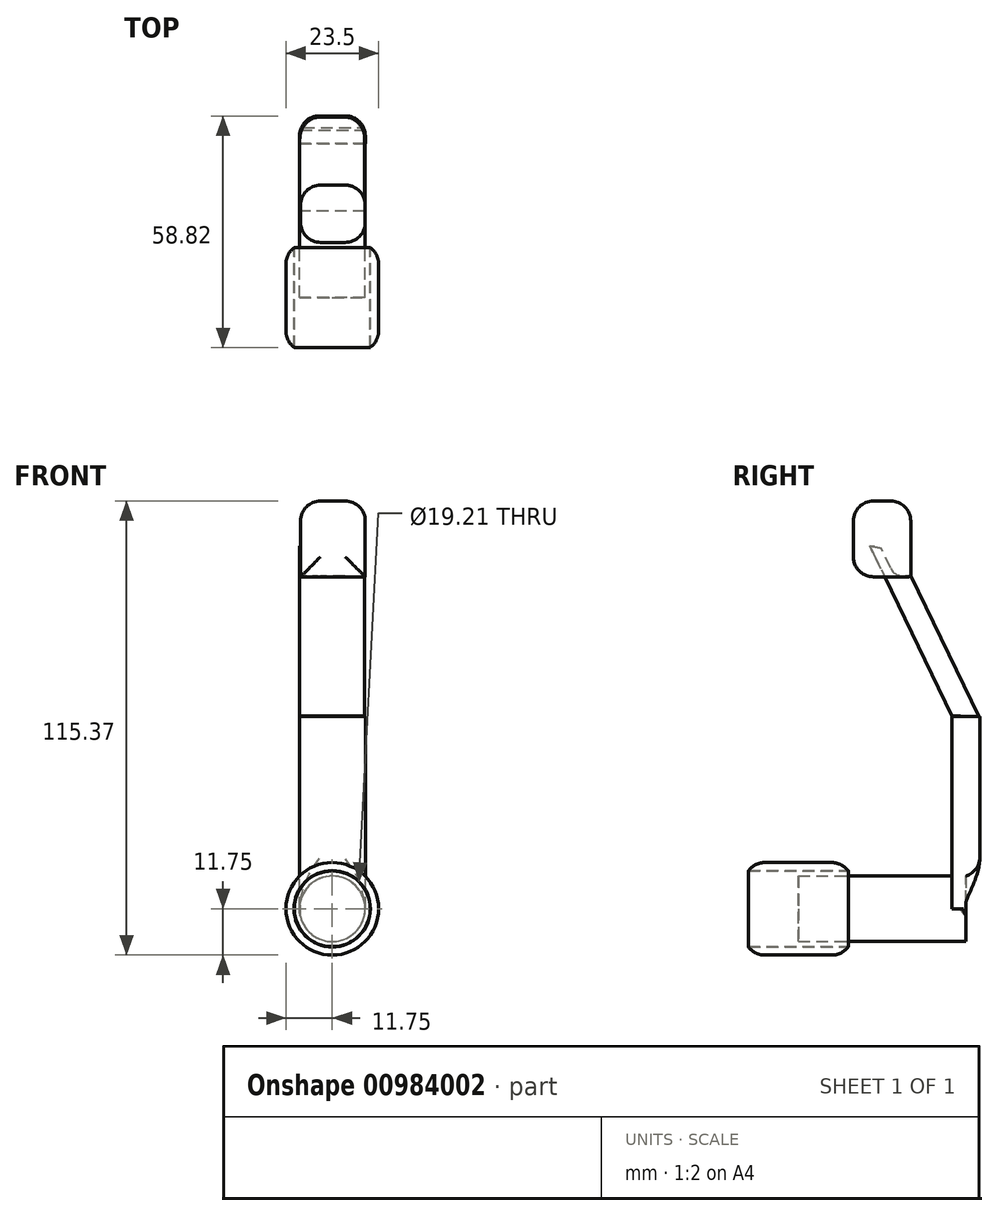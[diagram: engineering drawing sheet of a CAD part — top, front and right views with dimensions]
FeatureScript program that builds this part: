
annotation { "Feature Type Name" : "Feature", "Feature Type Description" : "" }
export const myFeature = defineFeature(function(context is Context, id is Id, definition is map)
    precondition{}
    {
        {
            var Q0;
            Q0=qCreatedBy(makeId("Front.planeOp"),FACE);
            var sketch = newSketch(context, id + "F0", { "sketchPlane" : qUnion([Q0])});
            skCircle(sketch, "E0", {"center": v(0, 0) * mm, "radius": 8.33 * mm});
            skSolve(sketch);
        }
        {
            var Q0;
            Q0 = qSketchRegion(id + "F0", true);
            extrude(context, id + "F1", {"entities" : qUnion([Q0]), "endBound" : BoundingType.SYMMETRIC, "depth" : 42.58 * mm, "offsetDistance" : 25.4 * mm});
        }
        {
            var Q0;
            Q0=makeQuery(id+"F1.opExtrude","CAP_FACE",FACE,{"disambiguationData":[OSD([sQuery(id+"F0.wireOp",EDGE,"E0")])],"isStart":false});
            var sketch = newSketch(context, id + "F2", { "sketchPlane" : qUnion([Q0])});
            skCircle(sketch, "E1", {"center": v(0, 0) * mm, "radius": 11.75 * mm});
            skCircle(sketch, "E2", {"center": v(0, 0) * mm, "radius": 9.6 * mm});
            skSolve(sketch);
        }
        {
            var Q0;
            Q0 = qSketchRegion(id + "F2", true);
            extrude(context, id + "F3", {"entities" : qUnion([Q0]), "endBound" : BoundingType.SYMMETRIC, "depth" : 25.4 * mm, "offsetDistance" : 25.4 * mm});
        }
        {
            var Q0;
            Q0=makeQuery(id+"F1.opExtrude","CAP_FACE",FACE,{"disambiguationData":[OSD([sQuery(id+"F0.wireOp",EDGE,"E0")])],"isStart":false});
            var sketch = newSketch(context, id + "F4", { "sketchPlane" : qUnion([Q0])});
            skCircle(sketch, "E3", {"center": v(0, 0) * mm, "radius": 9.7 * mm});
            skSolve(sketch);
        }
        {
            var Q0;
            Q0 = qSketchRegion(id + "F4", true);
            extrude(context, id + "F5", {"entities" : qUnion([Q0]), "endBound" : BoundingType.SYMMETRIC, "depth" : 25.4 * mm, "offsetDistance" : 25.4 * mm});
        }
        {
            var Q0;
            Q0=makeQuery(id+"F3.opExtrude","CAP_EDGE",EDGE,{"disambiguationData":[OSD([sQuery(id+"F2.wireOp",EDGE,"E1")])],"isStart":false});
            var Q1;
            Q1=makeQuery(id+"F3.opExtrude","CAP_EDGE",EDGE,{"disambiguationData":[OSD([sQuery(id+"F2.wireOp",EDGE,"E1")])],"isStart":true});
            var Q2;
            Q2=makeQuery(id+"F3.opExtrude","SWEPT_FACE",FACE,{"disambiguationData":[OSD([sQuery(id+"F2.wireOp",EDGE,"E1")])]});
            fillet(context, id + "F6", {"entities" : qUnion([Q0, Q1, Q2]), "radius" : 5.08 * mm, "tangentPropagation" : true, "allowEdgeOverflow" : false});
        }
        {
            var Q0;
            Q0=makeQuery(id+"F1.opExtrude","CAP_FACE",FACE,{"disambiguationData":[OSD([sQuery(id+"F0.wireOp",EDGE,"E0")])],"isStart":true});
            var sketch = newSketch(context, id + "F7", { "sketchPlane" : qUnion([Q0])});
            skLineSegment(sketch, "E4.bottom", {"start": v(8.33, 0) * mm, "end": v(-8.4, 0) * mm});
            skLineSegment(sketch, "E4.top", {"start": v(8.33, 48.86) * mm, "end": v(-8.4, 48.86) * mm});
            skLineSegment(sketch, "E4.left", {"start": v(8.33, 0) * mm, "end": v(8.33, 48.86) * mm});
            skLineSegment(sketch, "E4.right", {"start": v(-8.4, 0) * mm, "end": v(-8.4, 48.86) * mm});
            skSolve(sketch);
        }
        {
            var Q0;
            Q0=makeQuery(id+"F7.imprint","IMPRINT",FACE,{"disambiguationData":[TD([[makeQuery(id+"F7.imprint","IMPRINT",EDGE,{"derivedFrom":sQuery(id+"F7.wireOp",EDGE,"E4.top")}),1.0]])]});
            extrude(context, id + "F8", {"entities" : qUnion([Q0]), "operationType" : NewBodyOperationType.ADD, "endBound" : BoundingType.SYMMETRIC, "oppositeDirection" : true, "depth" : 7.08 * mm, "offsetDistance" : 25.4 * mm});
        }
        {
            var Q0;
            Q0=qCreatedBy(makeId("Right.planeOp"),FACE);
            var sketch = newSketch(context, id + "F9", { "sketchPlane" : qUnion([Q0])});
            skLineSegment(sketch, "E5", {"start": v(24.62, 48.75) * mm, "end": v(4.26, 90.83) * mm});
            skLineSegment(sketch, "E6", {"start": v(17.76, 49.04) * mm, "end": v(-3.14, 92.24) * mm});
            skLineSegment(sketch, "E7", {"start": v(4.26, 90.83) * mm, "end": v(-3.14, 92.24) * mm});
            skLineSegment(sketch, "E8", {"start": v(24.62, 48.75) * mm, "end": v(17.76, 49.04) * mm});
            skSolve(sketch);
        }
        {
            var Q0;
            Q0 = qSketchRegion(id + "F9", true);
            extrude(context, id + "F10", {"entities" : qUnion([Q0]), "operationType" : NewBodyOperationType.ADD, "endBound" : BoundingType.SYMMETRIC, "depth" : 16.5 * mm, "offsetDistance" : 25.4 * mm});
        }
        {
            var Q0;
            Q0=qCreatedBy(makeId("Front.planeOp"),FACE);
            var sketch = newSketch(context, id + "F11", { "sketchPlane" : qUnion([Q0])});
            skLineSegment(sketch, "E9.bottom", {"start": v(-8.06, 84.36) * mm, "end": v(8.38, 84.36) * mm});
            skLineSegment(sketch, "E9.top", {"start": v(-8.06, 103.62) * mm, "end": v(8.38, 103.62) * mm});
            skLineSegment(sketch, "E9.left", {"start": v(-8.06, 84.36) * mm, "end": v(-8.06, 103.62) * mm});
            skLineSegment(sketch, "E9.right", {"start": v(8.38, 84.36) * mm, "end": v(8.38, 103.62) * mm});
            skSolve(sketch);
        }
        {
            var Q0;
            Q0 = qSketchRegion(id + "F11", true);
            extrude(context, id + "F12", {"entities" : qUnion([Q0]), "operationType" : NewBodyOperationType.ADD, "endBound" : BoundingType.SYMMETRIC, "depth" : 14.56 * mm, "offsetDistance" : 25.4 * mm});
        }
        {
            var Q0;
            Q0=makeQuery(id+"F10.opExtrude","CAP_EDGE",EDGE,{"disambiguationData":[OSD([sQuery(id+"F9.wireOp",EDGE,"E5")])],"isStart":false});
            var Q1;
            Q1=makeQuery(id+"F10.opExtrude","CAP_EDGE",EDGE,{"disambiguationData":[OSD([sQuery(id+"F9.wireOp",EDGE,"E5")])],"isStart":true});
            fillet(context, id + "F13", {"entities" : qUnion([Q0, Q1]), "radius" : 5.08 * mm, "tangentPropagation" : true, "allowEdgeOverflow" : false});
        }
        {
            var Q0;
            Q0=makeQuery(id+"F8.opExtrude","CAP_EDGE",EDGE,{"disambiguationData":[OSD([sQuery(id+"F7.wireOp",EDGE,"E4.right")])],"isStart":true});
            var Q1;
            Q1=makeQuery(id+"F8.opExtrude","CAP_EDGE",EDGE,{"disambiguationData":[OSD([sQuery(id+"F7.wireOp",EDGE,"E4.left")])],"isStart":true});
            fillet(context, id + "F14", {"entities" : qUnion([Q0, Q1]), "radius" : 5.08 * mm, "tangentPropagation" : true, "allowEdgeOverflow" : false});
        }
        {
            var Q0;
            Q0=makeQuery(id+"F12.opExtrude","CAP_EDGE",EDGE,{"disambiguationData":[OSD([sQuery(id+"F11.wireOp",EDGE,"E9.left")])],"isStart":true});
            var Q1;
            Q1=makeQuery(id+"F12.opExtrude","CAP_EDGE",EDGE,{"disambiguationData":[OSD([sQuery(id+"F11.wireOp",EDGE,"E9.right")])],"isStart":true});
            var Q2;
            Q2=makeQuery(id+"F12.opExtrude","CAP_EDGE",EDGE,{"disambiguationData":[OSD([sQuery(id+"F11.wireOp",EDGE,"E9.left")])],"isStart":false});
            var Q3;
            Q3=makeQuery(id+"F12.opExtrude","CAP_EDGE",EDGE,{"disambiguationData":[OSD([sQuery(id+"F11.wireOp",EDGE,"E9.right")])],"isStart":false});
            var Q4;
            Q4=makeQuery(id+"F12.opExtrude","SWEPT_EDGE",EDGE,{"disambiguationData":[OSD([sQuery(id+"F11.wireOp",EDGE,"E9.top"),sQuery(id+"F11.wireOp",EDGE,"E9.left")])]});
            var Q5;
            Q5=makeQuery(id+"F12.opExtrude","SWEPT_EDGE",EDGE,{"disambiguationData":[OSD([sQuery(id+"F11.wireOp",EDGE,"E9.top"),sQuery(id+"F11.wireOp",EDGE,"E9.right")])]});
            var Q6;
            Q6=makeQuery(id+"F12.opExtrude","CAP_EDGE",EDGE,{"disambiguationData":[OSD([sQuery(id+"F11.wireOp",EDGE,"E9.top")])],"isStart":true});
            var Q7;
            Q7=makeQuery(id+"F12.opExtrude","SWEPT_FACE",FACE,{"disambiguationData":[OSD([sQuery(id+"F11.wireOp",EDGE,"E9.top")])]});
            var Q8;
            Q8=makeQuery(id+"F12.opExtrude","CAP_EDGE",EDGE,{"disambiguationData":[OSD([sQuery(id+"F11.wireOp",EDGE,"E9.bottom")])],"isStart":false});
            fillet(context, id + "F15", {"entities" : qUnion([Q0, Q1, Q2, Q3, Q4, Q5, Q6, Q7, Q8]), "radius" : 5.08 * mm, "tangentPropagation" : true, "allowEdgeOverflow" : false});
        }
        {
            var Q0;
            Q0=makeQuery(id+"F8.opExtrude","CAP_EDGE",EDGE,{"disambiguationData":[OSD([sQuery(id+"F0.wireOp",EDGE,"E0")])],"isStart":true});
            fillet(context, id + "F16", {"entities" : qUnion([Q0]), "radius" : 5.08 * mm, "tangentPropagation" : true, "allowEdgeOverflow" : false});
        }
    });
